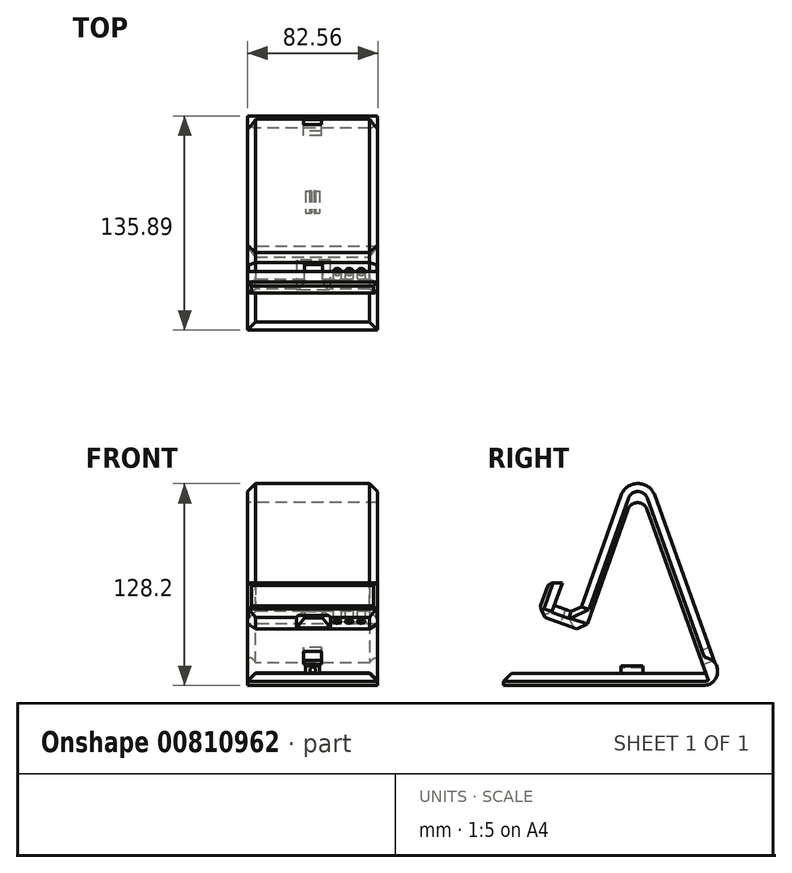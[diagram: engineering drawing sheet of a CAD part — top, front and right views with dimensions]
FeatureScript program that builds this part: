
annotation { "Feature Type Name" : "Feature", "Feature Type Description" : "" }
export const myFeature = defineFeature(function(context is Context, id is Id, definition is map)
    precondition{}
    {
        {
            var Q0;
            Q0=qCreatedBy(makeId("Right.planeOp"),FACE);
            var sketch = newSketch(context, id + "F0", { "sketchPlane" : qUnion([Q0])});
            skLineSegment(sketch, "E0", {"start": v(-74.4, -72.9) * mm, "end": v(-74.4, -65.28) * mm});
            skLineSegment(sketch, "E1", {"start": v(-74.4, -72.9) * mm, "end": v(52.6, -72.9) * mm});
            skArc(sketch, "E2", {"start": v(52.6, -72.9) * mm, "mid": v(60.54, -68) * mm, "end": v(59.72, -58.7) * mm});
            skArc(sketch, "E3", {"start": v(16.57, 38.98) * mm, "mid": v(10.6, 43.2) * mm, "end": v(4.6, 38.98) * mm});
            skLineSegment(sketch, "E4", {"start": v(4.6, 38.98) * mm, "end": v(-23.08, -38.79) * mm});
            skLineSegment(sketch, "E5", {"start": v(0, 47.7) * mm, "end": v(-26.77, -27.7) * mm});
            skLineSegment(sketch, "E6", {"start": v(-74.4, -65.28) * mm, "end": v(52.6, -65.28) * mm});
            skArc(sketch, "E7", {"start": v(52.6, -65.28) * mm, "mid": v(53.25, -65.21) * mm, "end": v(53.9, -65.02) * mm});
            skLineSegment(sketch, "E8", {"start": v(16.57, 38.98) * mm, "end": v(53.9, -65.02) * mm});
            skLineSegment(sketch, "E9", {"start": v(-26.77, -27.7) * mm, "end": v(-42.33, -22.18) * mm});
            skLineSegment(sketch, "E10", {"start": v(59.72, -58.7) * mm, "end": v(21.54, 47.7) * mm});
            skArc(sketch, "E11", {"start": v(21.54, 47.7) * mm, "mid": v(10.77, 55.3) * mm, "end": v(0, 47.7) * mm});
            skLineSegment(sketch, "E12", {"start": v(-23.08, -38.79) * mm, "end": v(-53, -28.16) * mm});
            skLineSegment(sketch, "E13", {"start": v(-53, -28.16) * mm, "end": v(-45.78, -7.82) * mm});
            skLineSegment(sketch, "E14", {"start": v(-42.33, -22.18) * mm, "end": v(-37.23, -7.82) * mm});
            skLineSegment(sketch, "E15", {"start": v(-37.23, -7.82) * mm, "end": v(-45.78, -7.82) * mm});
            skSolve(sketch);
        }
        {
            var Q0;
            Q0 = qSketchRegion(id + "F0", true);
            extrude(context, id + "F1", {"entities" : qUnion([Q0]), "endBound" : BoundingType.SYMMETRIC, "depth" : 82.55 * mm, "offsetDistance" : 25.4 * mm});
        }
        {
            var Q0;
            Q0=makeQuery(id+"F1.opExtrude","SWEPT_FACE",FACE,{"disambiguationData":[OSD([sQuery(id+"F0.wireOp",EDGE,"E10")])]});
            var sketch = newSketch(context, id + "F2", { "sketchPlane" : qUnion([Q0])});
            skLineSegment(sketch, "E16.bottom", {"start": v(-5.58, -64.86) * mm, "end": v(5.85, -64.86) * mm});
            skLineSegment(sketch, "E16.top", {"start": v(-5.58, -73.75) * mm, "end": v(5.85, -73.75) * mm});
            skLineSegment(sketch, "E16.left", {"start": v(-5.58, -64.86) * mm, "end": v(-5.58, -73.75) * mm});
            skLineSegment(sketch, "E16.right", {"start": v(5.85, -64.86) * mm, "end": v(5.85, -73.75) * mm});
            skSolve(sketch);
        }
        {
            var Q0;
            Q0=makeQuery(id+"F1.opExtrude","SWEPT_FACE",FACE,{"disambiguationData":[OSD([sQuery(id+"F0.wireOp",EDGE,"E12")])]});
            var sketch = newSketch(context, id + "F3", { "sketchPlane" : qUnion([Q0])});
            skLineSegment(sketch, "E17.bottom", {"start": v(-5.34, 32.47) * mm, "end": v(6.1, 32.47) * mm});
            skLineSegment(sketch, "E17.top", {"start": v(-5.34, 21.04) * mm, "end": v(6.1, 21.04) * mm});
            skLineSegment(sketch, "E17.left", {"start": v(-5.34, 32.47) * mm, "end": v(-5.34, 21.04) * mm});
            skLineSegment(sketch, "E17.right", {"start": v(6.1, 32.47) * mm, "end": v(6.1, 21.04) * mm});
            skSolve(sketch);
        }
        {
            var Q0;
            Q0 = qSketchRegion(id + "F3", true);
            extrude(context, id + "F4", {"entities" : qUnion([Q0]), "operationType" : NewBodyOperationType.REMOVE, "oppositeDirection" : true, "depth" : 25.4 * mm, "offsetDistance" : 25.4 * mm});
        }
        {
            var Q0;
            Q0=makeQuery(id+"F1.opExtrude","CAP_EDGE",EDGE,{"disambiguationData":[OSD([sQuery(id+"F0.wireOp",EDGE,"E11")])],"isStart":true});
            var Q1;
            Q1=makeQuery(id+"F1.opExtrude","CAP_EDGE",EDGE,{"disambiguationData":[OSD([sQuery(id+"F0.wireOp",EDGE,"E11")])],"isStart":false});
            var Q2;
            Q2=makeQuery(id+"F1.opExtrude","SWEPT_FACE",FACE,{"disambiguationData":[OSD([sQuery(id+"F0.wireOp",EDGE,"E5")])]});
            chamfer(context, id + "F5", {"entities" : qUnion([Q0, Q1, Q2]), "width" : 5.08 * mm, "tangentPropagation" : true});
        }
        {
            var Q0;
            Q0=makeQuery(id+"F1.opExtrude","CAP_EDGE",EDGE,{"disambiguationData":[OSD([sQuery(id+"F0.wireOp",EDGE,"E6")])],"isStart":true});
            var Q1;
            Q1=makeQuery(id+"F1.opExtrude","CAP_EDGE",EDGE,{"disambiguationData":[OSD([sQuery(id+"F0.wireOp",EDGE,"E6")])],"isStart":false});
            var Q2;
            Q2=makeQuery(id+"F1.opExtrude","SWEPT_EDGE",EDGE,{"disambiguationData":[OSD([sQuery(id+"F0.wireOp",EDGE,"E0"),sQuery(id+"F0.wireOp",EDGE,"E6")])]});
            chamfer(context, id + "F6", {"entities" : qUnion([Q0, Q1, Q2]), "width" : 5.08 * mm, "tangentPropagation" : true});
        }
        {
            var Q0;
            Q0=makeQuery(id+"F1.opExtrude","SWEPT_FACE",FACE,{"disambiguationData":[OSD([sQuery(id+"F0.wireOp",EDGE,"E12")])]});
            var Q1;
            Q1=makeQuery(id+"F1.opExtrude","SWEPT_FACE",FACE,{"disambiguationData":[OSD([sQuery(id+"F0.wireOp",EDGE,"M52L2vIO-uQhl-kVl0-gAhK-etbjmQ1NK6K1")])]});
            chamfer(context, id + "F7", {"entities" : qUnion([Q0, Q1]), "width" : 5.08 * mm, "tangentPropagation" : true});
        }
        {
            var Q0;
            Q0=makeQuery(id+"F1.opExtrude","SWEPT_FACE",FACE,{"disambiguationData":[OSD([sQuery(id+"F0.wireOp",EDGE,"E12")])]});
            var sketch = newSketch(context, id + "F8", { "sketchPlane" : qUnion([Q0])});
            skCircle(sketch, "E18", {"center": v(15.5, 27.43) * mm, "radius": 2.54 * mm});
            skCircle(sketch, "E19", {"center": v(23.13, 27.43) * mm, "radius": 2.54 * mm});
            skCircle(sketch, "E20", {"center": v(30.75, 27.43) * mm, "radius": 2.54 * mm});
            skSolve(sketch);
        }
        {
            var Q0;
            Q0 = qSketchRegion(id + "F8", true);
            extrude(context, id + "F9", {"entities" : qUnion([Q0]), "operationType" : NewBodyOperationType.REMOVE, "oppositeDirection" : true, "depth" : 25.4 * mm, "offsetDistance" : 25.4 * mm});
        }
        {
            var Q0;
            Q0 = qSketchRegion(id + "F2", true);
            extrude(context, id + "F10", {"entities" : qUnion([Q0]), "operationType" : NewBodyOperationType.REMOVE, "oppositeDirection" : true, "depth" : 20.32 * mm, "offsetDistance" : 25.4 * mm});
        }
        {
            var Q0;
            Q0=makeQuery(id+"F1.opExtrude","SWEPT_FACE",FACE,{"disambiguationData":[OSD([sQuery(id+"F0.wireOp",EDGE,"E13")])]});
            chamfer(context, id + "F11", {"entities" : qUnion([Q0]), "width" : 2.54 * mm, "tangentPropagation" : true});
        }
        {
            var Q0;
            Q0=qCreatedBy(makeId("Front.planeOp"),FACE);
            var sketch = newSketch(context, id + "F12", { "sketchPlane" : qUnion([Q0])});
            skLineSegment(sketch, "E21.bottom", {"start": v(-4.54, -59.7) * mm, "end": v(4.35, -59.7) * mm});
            skLineSegment(sketch, "E21.top", {"start": v(-4.54, -67.31) * mm, "end": v(4.35, -67.31) * mm});
            skLineSegment(sketch, "E21.left", {"start": v(-4.54, -59.7) * mm, "end": v(-4.54, -67.31) * mm});
            skLineSegment(sketch, "E21.right", {"start": v(4.35, -59.7) * mm, "end": v(4.35, -67.31) * mm});
            skCircle(sketch, "E22", {"center": v(0, -63.5) * mm, "radius": 1.9 * mm});
            skPoint(sketch, "E22.centerSnap0", {"position": v(-4.54, -63.5) * mm});
            skSolve(sketch);
        }
        {
            var Q0;
            Q0 = qSketchRegion(id + "F12", true);
            extrude(context, id + "F13", {"entities" : qUnion([Q0]), "operationType" : NewBodyOperationType.ADD, "oppositeDirection" : true, "depth" : 14 * mm, "offsetDistance" : 25.4 * mm});
        }
        {
            var Q0;
            Q0=makeQuery(id+"F13.opExtrude","CAP_FACE",FACE,{"disambiguationData":[OSD([sQuery(id+"F12.wireOp",EDGE,"E21.bottom"),sQuery(id+"F12.wireOp",EDGE,"E21.top"),sQuery(id+"F12.wireOp",EDGE,"E21.left"),sQuery(id+"F12.wireOp",EDGE,"E21.right"),sQuery(id+"F12.wireOp",EDGE,"E22")])],"isStart":true});
            var sketch = newSketch(context, id + "F14", { "sketchPlane" : qUnion([Q0])});
            skLineSegment(sketch, "E23", {"start": v(-0.89, -61.82) * mm, "end": v(-0.89, -59.7) * mm});
            skLineSegment(sketch, "E24", {"start": v(0, -61.6) * mm, "end": v(0, -59.7) * mm});
            skLineSegment(sketch, "E25", {"start": v(0.89, -61.82) * mm, "end": v(0.89, -59.7) * mm});
            skLineSegment(sketch, "E26", {"start": v(-0.89, -59.7) * mm, "end": v(0.89, -59.7) * mm});
            skLineSegment(sketch, "E27", {"start": v(-0.89, -61.82) * mm, "end": v(0.89, -61.82) * mm});
            skSolve(sketch);
        }
        {
            var Q0;
            Q0 = qSketchRegion(id + "F14", true);
            extrude(context, id + "F15", {"entities" : qUnion([Q0]), "operationType" : NewBodyOperationType.REMOVE, "oppositeDirection" : true, "depth" : 25.4 * mm, "offsetDistance" : 25.4 * mm});
        }
        {
            var Q0;
            {var subQ0=sQuery(id+"F12.wireOp",EDGE,"E22");var subQ1=sQuery(id+"F12.wireOp",EDGE,"E21.right");var subQ2=sQuery(id+"F12.wireOp",EDGE,"E21.bottom");Q0=makeQuery(id+"F15.boolean.opBoolean","SPLIT",FACE,{"disambiguationData":[TD([makeQuery(id+"F13.opExtrude","SWEPT_FACE",FACE,{"disambiguationData":[OSD([subQ1])]})])],"derivedFrom":makeQuery(id+"F13.opExtrude","CAP_FACE",FACE,{"disambiguationData":[OSD([subQ2,sQuery(id+"F12.wireOp",EDGE,"E21.top"),sQuery(id+"F12.wireOp",EDGE,"E21.left"),subQ1,subQ0])],"isStart":true})});}
            var sketch = newSketch(context, id + "F16", { "sketchPlane" : qUnion([Q0])});
            skLineSegment(sketch, "E28.bottom", {"start": v(-4.76, -58.53) * mm, "end": v(5.44, -58.53) * mm});
            skLineSegment(sketch, "E28.top", {"start": v(-4.76, -60.47) * mm, "end": v(5.44, -60.47) * mm});
            skLineSegment(sketch, "E28.left", {"start": v(-4.76, -58.53) * mm, "end": v(-4.76, -60.47) * mm});
            skLineSegment(sketch, "E28.right", {"start": v(5.44, -58.53) * mm, "end": v(5.44, -60.47) * mm});
            skSolve(sketch);
        }
        {
            var Q0;
            Q0 = qSketchRegion(id + "F16", true);
            extrude(context, id + "F17", {"entities" : qUnion([Q0]), "operationType" : NewBodyOperationType.REMOVE, "oppositeDirection" : true, "depth" : 25.4 * mm, "offsetDistance" : 25.4 * mm});
        }
    });
